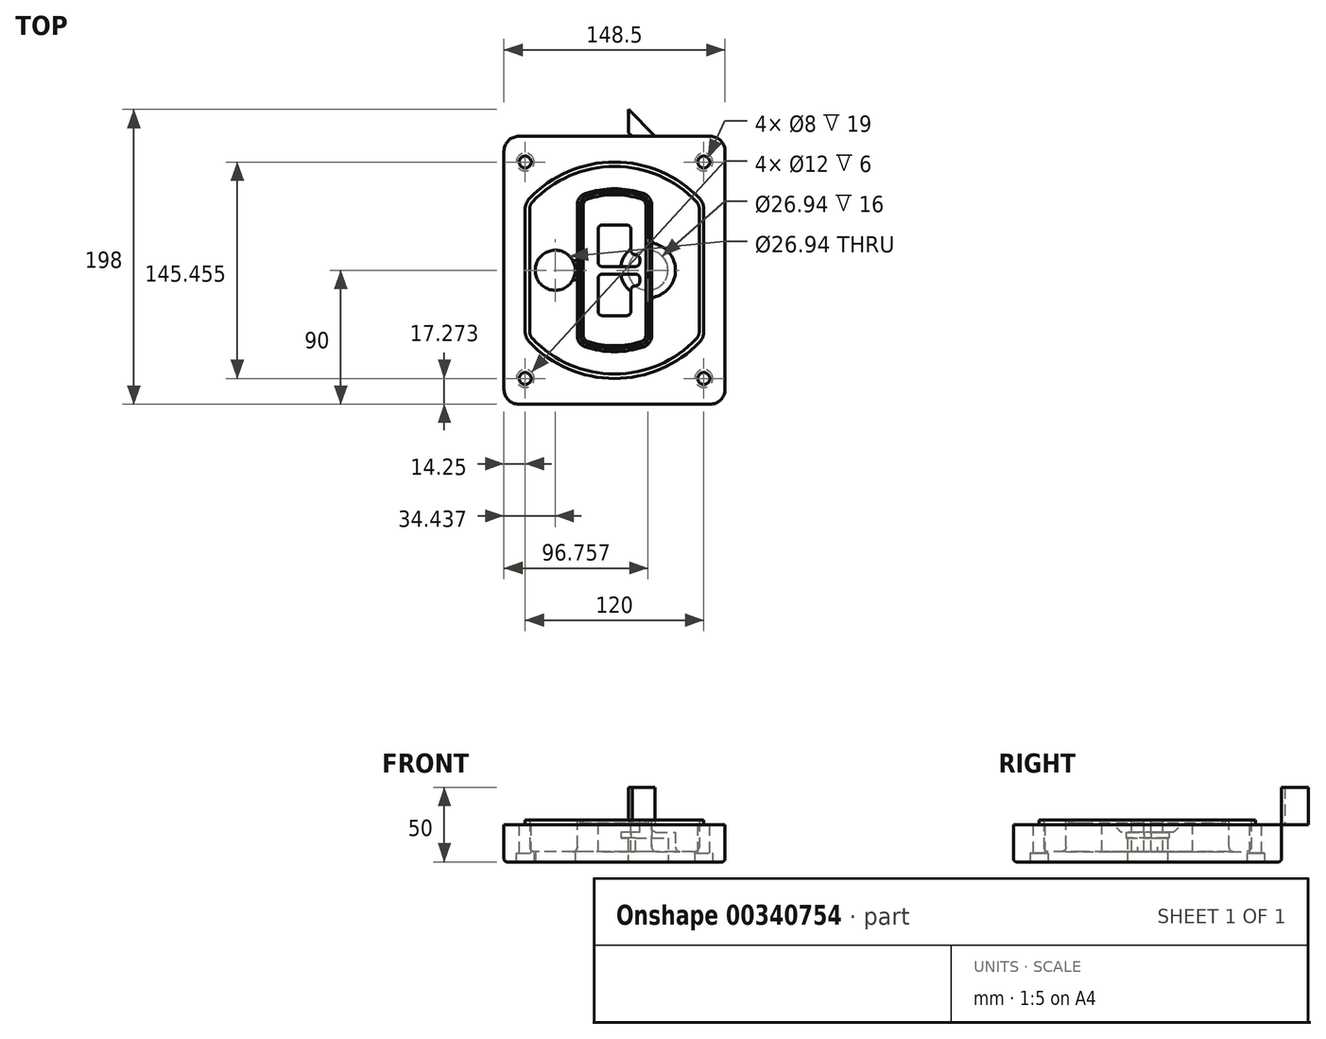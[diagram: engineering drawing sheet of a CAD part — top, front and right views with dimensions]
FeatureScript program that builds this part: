
annotation { "Feature Type Name" : "Feature", "Feature Type Description" : "" }
export const myFeature = defineFeature(function(context is Context, id is Id, definition is map)
    precondition{}
    {
        {
            var Q0;
            Q0=qCreatedBy(makeId("Top.planeOp"),FACE);
            var sketch = newSketch(context, id + "F0", { "sketchPlane" : qUnion([Q0])});
            skPoint(sketch, "E0.rect.middle", {"position": v(0, 0) * mm});
            skLineSegment(sketch, "E1.bottom", {"start": v(-64.25, -90) * mm, "end": v(64.25, -90) * mm});
            skLineSegment(sketch, "E1.top", {"start": v(-64.25, 90) * mm, "end": v(64.25, 90) * mm});
            skLineSegment(sketch, "E1.left", {"start": v(-74.25, -80) * mm, "end": v(-74.25, 80) * mm});
            skLineSegment(sketch, "E1.right", {"start": v(74.25, -80) * mm, "end": v(74.25, 80) * mm});
            skLineSegment(sketch, "E2", {"start": v(-74.25, 90) * mm, "end": v(74.25, -90) * mm, "construction": true});
            skLineSegment(sketch, "E3", {"start": v(74.25, 90) * mm, "end": v(-74.25, -90) * mm, "construction": true});
            skCircle(sketch, "E4", {"center": v(-60, 72.73) * mm, "radius": 4 * mm});
            skCircle(sketch, "E5", {"center": v(60, 72.73) * mm, "radius": 4 * mm});
            skCircle(sketch, "E6", {"center": v(60, -72.73) * mm, "radius": 4 * mm});
            skCircle(sketch, "E7", {"center": v(-60, -72.73) * mm, "radius": 4 * mm});
            skLineSegment(sketch, "E8", {"start": v(-60, 72.73) * mm, "end": v(60, 72.73) * mm, "construction": true});
            skLineSegment(sketch, "E9", {"start": v(60, 72.73) * mm, "end": v(60, -72.73) * mm, "construction": true});
            skLineSegment(sketch, "E10", {"start": v(60, -72.73) * mm, "end": v(-60, -72.73) * mm, "construction": true});
            skLineSegment(sketch, "E11", {"start": v(-60, -72.73) * mm, "end": v(-60, 72.73) * mm, "construction": true});
            skLineSegment(sketch, "E12", {"start": v(-60, 41.18) * mm, "end": v(-60, -41.18) * mm});
            skLineSegment(sketch, "E13", {"start": v(60, 41.18) * mm, "end": v(60, -41.18) * mm});
            skArc(sketch, "E14", {"start": v(57.27, 48.05) * mm, "mid": v(0, 72.73) * mm, "end": v(-57.27, 48.05) * mm});
            skArc(sketch, "E15", {"start": v(-57.27, -48.05) * mm, "mid": v(0, -72.73) * mm, "end": v(57.27, -48.05) * mm});
            skLineSegment(sketch, "E16", {"start": v(-60, 0) * mm, "end": v(60, 0) * mm, "construction": true});
            skPoint(sketch, "E17.visualSharp", {"position": v(-60, -45) * mm});
            skArc(sketch, "E17.filletArc", {"start": v(-60, -41.18) * mm, "mid": v(-59.3, -44.87) * mm, "end": v(-57.27, -48.05) * mm});
            skPoint(sketch, "E18.visualSharp", {"position": v(-60, 45) * mm});
            skArc(sketch, "E18.filletArc", {"start": v(-57.27, 48.05) * mm, "mid": v(-59.3, 44.87) * mm, "end": v(-60, 41.18) * mm});
            skPoint(sketch, "E19.visualSharp", {"position": v(60, 45) * mm});
            skArc(sketch, "E19.filletArc", {"start": v(60, 41.18) * mm, "mid": v(59.3, 44.87) * mm, "end": v(57.27, 48.05) * mm});
            skPoint(sketch, "E20.visualSharp", {"position": v(60, -45) * mm});
            skArc(sketch, "E20.filletArc", {"start": v(57.27, -48.05) * mm, "mid": v(59.3, -44.87) * mm, "end": v(60, -41.18) * mm});
            skPoint(sketch, "E21.visualSharp", {"position": v(-74.25, 90) * mm});
            skArc(sketch, "E21.filletArc", {"start": v(-64.25, 90) * mm, "mid": v(-71.32, 87.07) * mm, "end": v(-74.25, 80) * mm});
            skPoint(sketch, "E22.visualSharp", {"position": v(74.25, 90) * mm});
            skArc(sketch, "E22.filletArc", {"start": v(74.25, 80) * mm, "mid": v(71.32, 87.07) * mm, "end": v(64.25, 90) * mm});
            skPoint(sketch, "E23.visualSharp", {"position": v(74.25, -90) * mm});
            skArc(sketch, "E23.filletArc", {"start": v(64.25, -90) * mm, "mid": v(71.32, -87.07) * mm, "end": v(74.25, -80) * mm});
            skPoint(sketch, "E24.visualSharp", {"position": v(-74.25, -90) * mm});
            skArc(sketch, "E24.filletArc", {"start": v(-74.25, -80) * mm, "mid": v(-71.32, -87.07) * mm, "end": v(-64.25, -90) * mm});
            skArc(sketch, "E25.0", {"start": v(57, 41.18) * mm, "mid": v(56.5, 43.76) * mm, "end": v(55.09, 45.99) * mm});
            skLineSegment(sketch, "E25.1", {"start": v(57, 41.18) * mm, "end": v(57, -41.18) * mm});
            skArc(sketch, "E25.2", {"start": v(55.09, -45.99) * mm, "mid": v(56.5, -43.76) * mm, "end": v(57, -41.18) * mm});
            skArc(sketch, "E25.3", {"start": v(-55.09, -45.99) * mm, "mid": v(0, -69.73) * mm, "end": v(55.09, -45.99) * mm});
            skArc(sketch, "E25.4", {"start": v(-57, -41.18) * mm, "mid": v(-56.5, -43.76) * mm, "end": v(-55.09, -45.99) * mm});
            skArc(sketch, "E25.5", {"start": v(55.09, 45.99) * mm, "mid": v(0, 69.73) * mm, "end": v(-55.09, 45.99) * mm});
            skLineSegment(sketch, "E25.6", {"start": v(-57, 41.18) * mm, "end": v(-57, -41.18) * mm});
            skArc(sketch, "E25.7", {"start": v(-55.09, 45.99) * mm, "mid": v(-56.5, 43.76) * mm, "end": v(-57, 41.18) * mm});
            skArc(sketch, "E26.0", {"start": v(-60.18, 50.8) * mm, "mid": v(-63, 46.35) * mm, "end": v(-64, 41.18) * mm});
            skArc(sketch, "E26.1", {"start": v(60.18, 50.8) * mm, "mid": v(0, 76.73) * mm, "end": v(-60.18, 50.8) * mm});
            skArc(sketch, "E26.2", {"start": v(64, 41.18) * mm, "mid": v(63, 46.35) * mm, "end": v(60.18, 50.8) * mm});
            skLineSegment(sketch, "E26.3", {"start": v(64, 41.18) * mm, "end": v(64, -41.18) * mm});
            skArc(sketch, "E26.4", {"start": v(60.18, -50.8) * mm, "mid": v(63, -46.35) * mm, "end": v(64, -41.18) * mm});
            skLineSegment(sketch, "E26.5", {"start": v(-64, 41.18) * mm, "end": v(-64, -41.18) * mm});
            skArc(sketch, "E26.6", {"start": v(-60.18, -50.8) * mm, "mid": v(0, -76.73) * mm, "end": v(60.18, -50.8) * mm});
            skArc(sketch, "E26.7", {"start": v(-64, -41.18) * mm, "mid": v(-63, -46.35) * mm, "end": v(-60.18, -50.8) * mm});
            skSolve(sketch);
        }
        {
            var Q0;
            Q0=makeQuery(id+"F0.imprint","IMPRINT",FACE,{"disambiguationData":[TD([[makeQuery(id+"F0.imprint","IMPRINT",EDGE,{"derivedFrom":sQuery(id+"F0.wireOp",EDGE,"E1.bottom")}),1.0]])]});
            var Q1;
            Q1=makeQuery(id+"F0.imprint","IMPRINT",FACE,{"disambiguationData":[TD([[makeQuery(id+"F0.imprint","IMPRINT",EDGE,{"derivedFrom":sQuery(id+"F0.wireOp",EDGE,"E12")}),1.0]])]});
            var Q2;
            Q2=makeQuery(id+"F0.imprint","IMPRINT",FACE,{"disambiguationData":[TD([[makeQuery(id+"F0.imprint","IMPRINT",EDGE,{"derivedFrom":sQuery(id+"F0.wireOp",EDGE,"E25.0")}),1.0]])]});
            var Q3;
            Q3=makeQuery(id+"F0.imprint","IMPRINT",FACE,{"disambiguationData":[TD([[makeQuery(id+"F0.imprint","IMPRINT",EDGE,{"derivedFrom":sQuery(id+"F0.wireOp",EDGE,"E12")}),-1.0]])]});
            extrude(context, id + "F1", {"entities" : qUnion([Q0, Q1, Q2, Q3]), "oppositeDirection" : true, "depth" : 25 * mm});
        }
        {
            var Q0;
            Q0=makeQuery(id+"F0.imprint","IMPRINT",FACE,{"disambiguationData":[TD([[makeQuery(id+"F0.imprint","IMPRINT",EDGE,{"derivedFrom":sQuery(id+"F0.wireOp",EDGE,"E12")}),1.0]])]});
            extrude(context, id + "F2", {"entities" : qUnion([Q0]), "operationType" : NewBodyOperationType.ADD, "depth" : 3 * mm});
        }
        {
            var Q0;
            Q0=makeQuery(id+"F0.imprint","IMPRINT",FACE,{"disambiguationData":[TD([[makeQuery(id+"F0.imprint","IMPRINT",EDGE,{"derivedFrom":sQuery(id+"F0.wireOp",EDGE,"E25.0")}),1.0]])]});
            extrude(context, id + "F3", {"entities" : qUnion([Q0]), "operationType" : NewBodyOperationType.REMOVE, "oppositeDirection" : true, "depth" : 18 * mm});
        }
        {
            var Q0;
            Q0=makeQuery(id+"F2.opExtrude","CAP_FACE",FACE,{"disambiguationData":[OSD([sQuery(id+"F0.wireOp",EDGE,"E12"),sQuery(id+"F0.wireOp",EDGE,"E13"),sQuery(id+"F0.wireOp",EDGE,"E14"),sQuery(id+"F0.wireOp",EDGE,"E15"),sQuery(id+"F0.wireOp",EDGE,"E17.filletArc"),sQuery(id+"F0.wireOp",EDGE,"E18.filletArc"),sQuery(id+"F0.wireOp",EDGE,"E19.filletArc"),sQuery(id+"F0.wireOp",EDGE,"E20.filletArc"),sQuery(id+"F0.wireOp",EDGE,"E25.0"),sQuery(id+"F0.wireOp",EDGE,"E25.1"),sQuery(id+"F0.wireOp",EDGE,"E25.2"),sQuery(id+"F0.wireOp",EDGE,"E25.3"),sQuery(id+"F0.wireOp",EDGE,"E25.4"),sQuery(id+"F0.wireOp",EDGE,"E25.5"),sQuery(id+"F0.wireOp",EDGE,"E25.6"),sQuery(id+"F0.wireOp",EDGE,"E25.7")])],"isStart":false});
            var sketch = newSketch(context, id + "F4", { "sketchPlane" : qUnion([Q0])});
            skArc(sketch, "E27.0", {"start": v(-19.58, -51.49) * mm, "mid": v(0, -54.73) * mm, "end": v(19.58, -51.49) * mm});
            skArc(sketch, "E28.0", {"start": v(19.58, 51.49) * mm, "mid": v(0, 54.73) * mm, "end": v(-19.58, 51.49) * mm});
            skLineSegment(sketch, "E29", {"start": v(-25, 43.91) * mm, "end": v(-25, -43.91) * mm});
            skLineSegment(sketch, "E30", {"start": v(25, 43.91) * mm, "end": v(25, -43.91) * mm});
            skLineSegment(sketch, "E31", {"start": v(-25, 49.35) * mm, "end": v(25, 49.35) * mm, "construction": true});
            skLineSegment(sketch, "E32", {"start": v(-25, -49.35) * mm, "end": v(25, -49.35) * mm, "construction": true});
            skPoint(sketch, "E33.visualSharp", {"position": v(-25, 49.35) * mm});
            skArc(sketch, "E33.filletArc", {"start": v(-19.58, 51.49) * mm, "mid": v(-23.5, 48.57) * mm, "end": v(-25, 43.91) * mm});
            skPoint(sketch, "E34.visualSharp", {"position": v(25, 49.35) * mm});
            skArc(sketch, "E34.filletArc", {"start": v(25, 43.91) * mm, "mid": v(23.5, 48.57) * mm, "end": v(19.58, 51.49) * mm});
            skPoint(sketch, "E35.visualSharp", {"position": v(25, -49.35) * mm});
            skArc(sketch, "E35.filletArc", {"start": v(19.58, -51.49) * mm, "mid": v(23.5, -48.57) * mm, "end": v(25, -43.91) * mm});
            skPoint(sketch, "E36.visualSharp", {"position": v(-25, -49.35) * mm});
            skArc(sketch, "E36.filletArc", {"start": v(-25, -43.91) * mm, "mid": v(-23.5, -48.57) * mm, "end": v(-19.58, -51.49) * mm});
            skArc(sketch, "E37.0", {"start": v(55.09, 45.99) * mm, "mid": v(0, 69.73) * mm, "end": v(-55.09, 45.99) * mm});
            skArc(sketch, "E37.1", {"start": v(-55.09, 45.99) * mm, "mid": v(-56.5, 43.76) * mm, "end": v(-57, 41.18) * mm});
            skLineSegment(sketch, "E37.2", {"start": v(-57, 41.18) * mm, "end": v(-57, -41.18) * mm});
            skArc(sketch, "E37.3", {"start": v(-57, -41.18) * mm, "mid": v(-56.5, -43.76) * mm, "end": v(-55.09, -45.99) * mm});
            skArc(sketch, "E37.4", {"start": v(-55.09, -45.99) * mm, "mid": v(0, -69.73) * mm, "end": v(55.09, -45.99) * mm});
            skArc(sketch, "E37.5", {"start": v(55.09, -45.99) * mm, "mid": v(56.5, -43.76) * mm, "end": v(57, -41.18) * mm});
            skLineSegment(sketch, "E37.6", {"start": v(57, 41.18) * mm, "end": v(57, -41.18) * mm});
            skArc(sketch, "E37.7", {"start": v(57, 41.18) * mm, "mid": v(56.5, 43.76) * mm, "end": v(55.09, 45.99) * mm});
            skLineSegment(sketch, "E38.0", {"start": v(23, 43.91) * mm, "end": v(23, -43.91) * mm});
            skArc(sketch, "E38.1", {"start": v(18.93, -49.6) * mm, "mid": v(21.88, -47.4) * mm, "end": v(23, -43.91) * mm});
            skArc(sketch, "E38.2", {"start": v(-18.93, -49.6) * mm, "mid": v(0, -52.73) * mm, "end": v(18.93, -49.6) * mm});
            skArc(sketch, "E38.3", {"start": v(-23, -43.91) * mm, "mid": v(-21.88, -47.4) * mm, "end": v(-18.93, -49.6) * mm});
            skLineSegment(sketch, "E38.4", {"start": v(-23, 43.91) * mm, "end": v(-23, -43.91) * mm});
            skArc(sketch, "E38.5", {"start": v(23, 43.91) * mm, "mid": v(21.88, 47.4) * mm, "end": v(18.93, 49.6) * mm});
            skArc(sketch, "E38.6", {"start": v(-18.93, 49.6) * mm, "mid": v(-21.88, 47.4) * mm, "end": v(-23, 43.91) * mm});
            skArc(sketch, "E38.7", {"start": v(18.93, 49.6) * mm, "mid": v(0, 52.73) * mm, "end": v(-18.93, 49.6) * mm});
            skArc(sketch, "E39.0", {"start": v(21, 43.91) * mm, "mid": v(20.25, 46.24) * mm, "end": v(18.29, 47.7) * mm});
            skLineSegment(sketch, "E39.1", {"start": v(21, 43.91) * mm, "end": v(21, -43.91) * mm});
            skArc(sketch, "E39.2", {"start": v(18.29, -47.7) * mm, "mid": v(20.25, -46.24) * mm, "end": v(21, -43.91) * mm});
            skArc(sketch, "E39.3", {"start": v(-18.29, -47.7) * mm, "mid": v(0, -50.73) * mm, "end": v(18.29, -47.7) * mm});
            skArc(sketch, "E39.4", {"start": v(-21, -43.91) * mm, "mid": v(-20.25, -46.24) * mm, "end": v(-18.29, -47.7) * mm});
            skArc(sketch, "E39.5", {"start": v(18.29, 47.7) * mm, "mid": v(0, 50.73) * mm, "end": v(-18.29, 47.7) * mm});
            skLineSegment(sketch, "E39.6", {"start": v(-21, 43.91) * mm, "end": v(-21, -43.91) * mm});
            skArc(sketch, "E39.7", {"start": v(-18.29, 47.7) * mm, "mid": v(-20.25, 46.24) * mm, "end": v(-21, 43.91) * mm});
            skLineSegment(sketch, "E40", {"start": v(-25, 0) * mm, "end": v(25, 0) * mm, "construction": true});
            skLineSegment(sketch, "E41", {"start": v(-11, 5.5) * mm, "end": v(-11, 27.5) * mm});
            skLineSegment(sketch, "E42", {"start": v(-8, 30.5) * mm, "end": v(8, 30.5) * mm});
            skLineSegment(sketch, "E43", {"start": v(11, 27.5) * mm, "end": v(11, 13.5) * mm});
            skLineSegment(sketch, "E44", {"start": v(14, 10.5) * mm, "end": v(14, 10.5) * mm});
            skLineSegment(sketch, "E45", {"start": v(17, 7.5) * mm, "end": v(17, 5.5) * mm});
            skLineSegment(sketch, "E46", {"start": v(14, 2.5) * mm, "end": v(-8, 2.5) * mm});
            skPoint(sketch, "E47.visualSharp", {"position": v(-11, 30.5) * mm});
            skArc(sketch, "E47.filletArc", {"start": v(-8, 30.5) * mm, "mid": v(-10.12, 29.62) * mm, "end": v(-11, 27.5) * mm});
            skPoint(sketch, "E48.visualSharp", {"position": v(11, 30.5) * mm});
            skArc(sketch, "E48.filletArc", {"start": v(11, 27.5) * mm, "mid": v(10.12, 29.62) * mm, "end": v(8, 30.5) * mm});
            skPoint(sketch, "E49.visualSharp", {"position": v(11, 10.5) * mm});
            skArc(sketch, "E49.filletArc", {"start": v(11, 13.5) * mm, "mid": v(11.88, 11.38) * mm, "end": v(14, 10.5) * mm});
            skPoint(sketch, "E50.visualSharp", {"position": v(17, 10.5) * mm});
            skArc(sketch, "E50.filletArc", {"start": v(17, 7.5) * mm, "mid": v(16.12, 9.62) * mm, "end": v(14, 10.5) * mm});
            skPoint(sketch, "E51.visualSharp", {"position": v(17, 2.5) * mm});
            skArc(sketch, "E51.filletArc", {"start": v(14, 2.5) * mm, "mid": v(16.12, 3.38) * mm, "end": v(17, 5.5) * mm});
            skPoint(sketch, "E52.visualSharp", {"position": v(-11, 2.5) * mm});
            skArc(sketch, "E52.filletArc", {"start": v(-11, 5.5) * mm, "mid": v(-10.12, 3.38) * mm, "end": v(-8, 2.5) * mm});
            skLineSegment(sketch, "E53.0.MirrorCS", {"start": v(14, -2.5) * mm, "end": v(-8, -2.5) * mm});
            skArc(sketch, "E54.0.MirrorCS", {"start": v(-11, -5.5) * mm, "mid": v(-10.12, -3.38) * mm, "end": v(-8, -2.5) * mm});
            skLineSegment(sketch, "E55.0.MirrorCS", {"start": v(-11, -5.5) * mm, "end": v(-11, -27.5) * mm});
            skArc(sketch, "E56.0.MirrorCS", {"start": v(-8, -30.5) * mm, "mid": v(-10.12, -29.62) * mm, "end": v(-11, -27.5) * mm});
            skLineSegment(sketch, "E57.0.MirrorCS", {"start": v(-8, -30.5) * mm, "end": v(8, -30.5) * mm});
            skArc(sketch, "E58.0.MirrorCS", {"start": v(11, -27.5) * mm, "mid": v(10.12, -29.62) * mm, "end": v(8, -30.5) * mm});
            skLineSegment(sketch, "E59.0.MirrorCS", {"start": v(11, -27.5) * mm, "end": v(11, -13.5) * mm});
            skArc(sketch, "E60.0.MirrorCS", {"start": v(11, -13.5) * mm, "mid": v(11.88, -11.38) * mm, "end": v(14, -10.5) * mm});
            skArc(sketch, "E61.0.MirrorCS", {"start": v(17, -7.5) * mm, "mid": v(16.12, -9.62) * mm, "end": v(14, -10.5) * mm});
            skLineSegment(sketch, "E62.0.MirrorCS", {"start": v(17, -7.5) * mm, "end": v(17, -5.5) * mm});
            skArc(sketch, "E63.0.MirrorCS", {"start": v(14, -2.5) * mm, "mid": v(16.12, -3.38) * mm, "end": v(17, -5.5) * mm});
            skSolve(sketch);
        }
        {
            var Q0;
            Q0=makeQuery(id+"F4.imprint","IMPRINT",FACE,{"disambiguationData":[TD([[makeQuery(id+"F4.imprint","IMPRINT",EDGE,{"derivedFrom":sQuery(id+"F4.wireOp",EDGE,"E27.0")}),1.0]])]});
            var Q1;
            Q1=makeQuery(id+"F4.imprint","IMPRINT",FACE,{"disambiguationData":[TD([[makeQuery(id+"F4.imprint","IMPRINT",EDGE,{"derivedFrom":sQuery(id+"F4.wireOp",EDGE,"E38.0")}),-1.0]])]});
            var Q2;
            Q2=makeQuery(id+"F4.imprint","IMPRINT",FACE,{"disambiguationData":[TD([[makeQuery(id+"F4.imprint","IMPRINT",EDGE,{"derivedFrom":sQuery(id+"F4.wireOp",EDGE,"E39.0")}),1.0]])]});
            extrude(context, id + "F5", {"entities" : qUnion([Q0, Q1, Q2]), "operationType" : NewBodyOperationType.ADD, "endBound" : BoundingType.UP_TO_NEXT, "oppositeDirection" : true, "depth" : 25 * mm});
        }
        {
            var Q0;
            Q0=makeQuery(id+"F4.imprint","IMPRINT",FACE,{"disambiguationData":[TD([[makeQuery(id+"F4.imprint","IMPRINT",EDGE,{"derivedFrom":sQuery(id+"F4.wireOp",EDGE,"E38.0")}),-1.0]])]});
            extrude(context, id + "F6", {"entities" : qUnion([Q0]), "operationType" : NewBodyOperationType.REMOVE, "oppositeDirection" : true, "depth" : 2 * mm});
        }
        {
            var Q0;
            Q0=makeQuery(id+"F1.opExtrude","CAP_FACE",FACE,{"disambiguationData":[OSD([sQuery(id+"F0.wireOp",EDGE,"E1.bottom"),sQuery(id+"F0.wireOp",EDGE,"E1.top"),sQuery(id+"F0.wireOp",EDGE,"E1.left"),sQuery(id+"F0.wireOp",EDGE,"E1.right"),sQuery(id+"F0.wireOp",EDGE,"E4"),sQuery(id+"F0.wireOp",EDGE,"E5"),sQuery(id+"F0.wireOp",EDGE,"E6"),sQuery(id+"F0.wireOp",EDGE,"E7"),sQuery(id+"F0.wireOp",EDGE,"E21.filletArc"),sQuery(id+"F0.wireOp",EDGE,"E22.filletArc"),sQuery(id+"F0.wireOp",EDGE,"E23.filletArc"),sQuery(id+"F0.wireOp",EDGE,"E24.filletArc")])],"isStart":false});
            var sketch = newSketch(context, id + "F7", { "sketchPlane" : qUnion([Q0])});
            skCircle(sketch, "E64", {"center": v(22.5, 0) * mm, "radius": 13.47 * mm});
            skCircle(sketch, "E65", {"center": v(-39.81, 0) * mm, "radius": 13.47 * mm});
            skLineSegment(sketch, "E66", {"start": v(74.25, 0) * mm, "end": v(-74.25, 0) * mm});
            skCircle(sketch, "E67", {"center": v(22.5, 0) * mm, "radius": 18.47 * mm});
            skCircle(sketch, "E68", {"center": v(60, -72.73) * mm, "radius": 6 * mm});
            skCircle(sketch, "E69", {"center": v(-60, -72.73) * mm, "radius": 6 * mm});
            skCircle(sketch, "E70", {"center": v(-60, 72.73) * mm, "radius": 6 * mm});
            skCircle(sketch, "E71", {"center": v(60, 72.73) * mm, "radius": 6 * mm});
            skSolve(sketch);
        }
        {
            var Q0;
            {var subQ1=sQuery(id+"F7.wireOp",EDGE,"E66");var subQ4=sQuery(id+"F7.wireOp",EDGE,"E64");var subQ6=makeQuery(id+"F7.imprint","INTERSECT",VERTEX,{"disambiguationData":[OD(0.0)],"derivedFrom":[subQ4,subQ1]});Q0=makeQuery(id+"F7.imprint","IMPRINT",FACE,{"disambiguationData":[TD([[makeQuery(id+"F7.imprint","IMPRINT",EDGE,{"disambiguationData":[TD([[subQ6,-1.0]])],"derivedFrom":subQ4}),-1.0]])]});}
            var Q1;
            {var subQ0=sQuery(id+"F7.wireOp",EDGE,"E66");var subQ1=sQuery(id+"F7.wireOp",EDGE,"E64");var subQ3=makeQuery(id+"F7.imprint","INTERSECT",VERTEX,{"disambiguationData":[OD(0.0)],"derivedFrom":[subQ1,subQ0]});Q1=makeQuery(id+"F7.imprint","IMPRINT",FACE,{"disambiguationData":[TD([[makeQuery(id+"F7.imprint","IMPRINT",EDGE,{"disambiguationData":[TD([[subQ3,-1.0]])],"derivedFrom":subQ1}),1.0]])]});}
            var Q2;
            {var subQ0=sQuery(id+"F7.wireOp",EDGE,"E66");var subQ1=sQuery(id+"F7.wireOp",EDGE,"E64");var subQ3=makeQuery(id+"F7.imprint","INTERSECT",VERTEX,{"disambiguationData":[OD(0.0)],"derivedFrom":[subQ1,subQ0]});Q2=makeQuery(id+"F7.imprint","IMPRINT",FACE,{"disambiguationData":[TD([[makeQuery(id+"F7.imprint","IMPRINT",EDGE,{"disambiguationData":[TD([[subQ3,1.0]])],"derivedFrom":subQ1}),1.0]])]});}
            var Q3;
            {var subQ1=sQuery(id+"F7.wireOp",EDGE,"E66");var subQ4=sQuery(id+"F7.wireOp",EDGE,"E64");var subQ6=makeQuery(id+"F7.imprint","INTERSECT",VERTEX,{"disambiguationData":[OD(0.0)],"derivedFrom":[subQ4,subQ1]});Q3=makeQuery(id+"F7.imprint","IMPRINT",FACE,{"disambiguationData":[TD([[makeQuery(id+"F7.imprint","IMPRINT",EDGE,{"disambiguationData":[TD([[subQ6,1.0]])],"derivedFrom":subQ4}),-1.0]])]});}
            extrude(context, id + "F8", {"entities" : qUnion([Q0, Q1, Q2, Q3]), "operationType" : NewBodyOperationType.ADD, "oppositeDirection" : true, "depth" : 20 * mm});
        }
        {
            var Q0;
            {var subQ0=sQuery(id+"F7.wireOp",EDGE,"E66");var subQ1=sQuery(id+"F7.wireOp",EDGE,"E64");var subQ3=makeQuery(id+"F7.imprint","INTERSECT",VERTEX,{"disambiguationData":[OD(0.0)],"derivedFrom":[subQ1,subQ0]});Q0=makeQuery(id+"F7.imprint","IMPRINT",FACE,{"disambiguationData":[TD([[makeQuery(id+"F7.imprint","IMPRINT",EDGE,{"disambiguationData":[TD([[subQ3,-1.0]])],"derivedFrom":subQ1}),1.0]])]});}
            var Q1;
            {var subQ0=sQuery(id+"F7.wireOp",EDGE,"E66");var subQ1=sQuery(id+"F7.wireOp",EDGE,"E64");var subQ3=makeQuery(id+"F7.imprint","INTERSECT",VERTEX,{"disambiguationData":[OD(0.0)],"derivedFrom":[subQ1,subQ0]});Q1=makeQuery(id+"F7.imprint","IMPRINT",FACE,{"disambiguationData":[TD([[makeQuery(id+"F7.imprint","IMPRINT",EDGE,{"disambiguationData":[TD([[subQ3,1.0]])],"derivedFrom":subQ1}),1.0]])]});}
            extrude(context, id + "F9", {"entities" : qUnion([Q0, Q1]), "operationType" : NewBodyOperationType.REMOVE, "oppositeDirection" : true, "depth" : 16 * mm});
        }
        {
            var Q0;
            {var subQ0=sQuery(id+"F7.wireOp",EDGE,"E66");var subQ1=sQuery(id+"F7.wireOp",EDGE,"E65");var subQ3=makeQuery(id+"F7.imprint","INTERSECT",VERTEX,{"disambiguationData":[OD(0.0)],"derivedFrom":[subQ1,subQ0]});Q0=makeQuery(id+"F7.imprint","IMPRINT",FACE,{"disambiguationData":[TD([[makeQuery(id+"F7.imprint","IMPRINT",EDGE,{"disambiguationData":[TD([[subQ3,-1.0]])],"derivedFrom":subQ1}),1.0]])]});}
            var Q1;
            {var subQ0=sQuery(id+"F7.wireOp",EDGE,"E66");var subQ1=sQuery(id+"F7.wireOp",EDGE,"E65");var subQ3=makeQuery(id+"F7.imprint","INTERSECT",VERTEX,{"disambiguationData":[OD(0.0)],"derivedFrom":[subQ1,subQ0]});Q1=makeQuery(id+"F7.imprint","IMPRINT",FACE,{"disambiguationData":[TD([[makeQuery(id+"F7.imprint","IMPRINT",EDGE,{"disambiguationData":[TD([[subQ3,1.0]])],"derivedFrom":subQ1}),1.0]])]});}
            extrude(context, id + "F10", {"entities" : qUnion([Q0, Q1]), "operationType" : NewBodyOperationType.REMOVE, "oppositeDirection" : true, "depth" : 25 * mm});
        }
        {
            var Q0;
            Q0=makeQuery(id+"F7.imprint","IMPRINT",FACE,{"disambiguationData":[TD([[makeQuery(id+"F7.imprint","IMPRINT",EDGE,{"derivedFrom":sQuery(id+"F7.wireOp",EDGE,"E68")}),1.0]])]});
            var Q1;
            Q1=makeQuery(id+"F7.imprint","IMPRINT",FACE,{"disambiguationData":[TD([[makeQuery(id+"F7.imprint","IMPRINT",EDGE,{"derivedFrom":makeQuery(id+"F1.opExtrude","CAP_EDGE",EDGE,{"disambiguationData":[OSD([sQuery(id+"F0.wireOp",EDGE,"E5")])],"isStart":false})}),-1.0]])]});
            var Q2;
            Q2=makeQuery(id+"F7.imprint","IMPRINT",FACE,{"disambiguationData":[TD([[makeQuery(id+"F7.imprint","IMPRINT",EDGE,{"derivedFrom":sQuery(id+"F7.wireOp",EDGE,"E69")}),1.0]])]});
            var Q3;
            Q3=makeQuery(id+"F7.imprint","IMPRINT",FACE,{"disambiguationData":[TD([[makeQuery(id+"F7.imprint","IMPRINT",EDGE,{"derivedFrom":makeQuery(id+"F1.opExtrude","CAP_EDGE",EDGE,{"disambiguationData":[OSD([sQuery(id+"F0.wireOp",EDGE,"E4")])],"isStart":false})}),-1.0]])]});
            var Q4;
            Q4=makeQuery(id+"F7.imprint","IMPRINT",FACE,{"disambiguationData":[TD([[makeQuery(id+"F7.imprint","IMPRINT",EDGE,{"derivedFrom":sQuery(id+"F7.wireOp",EDGE,"E70")}),1.0]])]});
            var Q5;
            Q5=makeQuery(id+"F7.imprint","IMPRINT",FACE,{"disambiguationData":[TD([[makeQuery(id+"F7.imprint","IMPRINT",EDGE,{"derivedFrom":makeQuery(id+"F1.opExtrude","CAP_EDGE",EDGE,{"disambiguationData":[OSD([sQuery(id+"F0.wireOp",EDGE,"E7")])],"isStart":false})}),-1.0]])]});
            var Q6;
            Q6=makeQuery(id+"F7.imprint","IMPRINT",FACE,{"disambiguationData":[TD([[makeQuery(id+"F7.imprint","IMPRINT",EDGE,{"derivedFrom":sQuery(id+"F7.wireOp",EDGE,"E71")}),1.0]])]});
            var Q7;
            Q7=makeQuery(id+"F7.imprint","IMPRINT",FACE,{"disambiguationData":[TD([[makeQuery(id+"F7.imprint","IMPRINT",EDGE,{"derivedFrom":makeQuery(id+"F1.opExtrude","CAP_EDGE",EDGE,{"disambiguationData":[OSD([sQuery(id+"F0.wireOp",EDGE,"E6")])],"isStart":false})}),-1.0]])]});
            extrude(context, id + "F11", {"entities" : qUnion([Q0, Q1, Q2, Q3, Q4, Q5, Q6, Q7]), "operationType" : NewBodyOperationType.REMOVE, "oppositeDirection" : true, "depth" : 6 * mm});
        }
        {
            var Q0;
            Q0=makeQuery(id+"F9.boolean.opBoolean","COPY",FACE,{"derivedFrom":makeQuery(id+"F9.opExtrude","CAP_FACE",FACE,{"disambiguationData":[OSD([sQuery(id+"F7.wireOp",EDGE,"E64")])],"isStart":false})});
            var sketch = newSketch(context, id + "F12", { "sketchPlane" : qUnion([Q0])});
            skArc(sketch, "E72.0", {"start": v(11, 14.45) * mm, "mid": v(6.45, 9.13) * mm, "end": v(4.2, 2.5) * mm});
            skArc(sketch, "E72.1", {"start": v(4.2, -2.5) * mm, "mid": v(6.45, -9.13) * mm, "end": v(11, -14.45) * mm});
            skLineSegment(sketch, "E73", {"start": v(4.2, -2.5) * mm, "end": v(14, -2.5) * mm});
            skLineSegment(sketch, "E74.0", {"start": v(14, 2.5) * mm, "end": v(4.2, 2.5) * mm});
            skArc(sketch, "E74.1", {"start": v(14, 2.5) * mm, "mid": v(16.12, 3.38) * mm, "end": v(17, 5.5) * mm});
            skLineSegment(sketch, "E74.2", {"start": v(17, 7.5) * mm, "end": v(17, 5.5) * mm});
            skArc(sketch, "E74.3", {"start": v(17, 7.5) * mm, "mid": v(16.12, 9.62) * mm, "end": v(14, 10.5) * mm});
            skArc(sketch, "E74.4", {"start": v(11, 13.5) * mm, "mid": v(11.88, 11.38) * mm, "end": v(14, 10.5) * mm});
            skLineSegment(sketch, "E74.5", {"start": v(11, 14.45) * mm, "end": v(11, 13.5) * mm});
            skLineSegment(sketch, "E74.7", {"start": v(14, -2.5) * mm, "end": v(4.2, -2.5) * mm});
            skArc(sketch, "E74.8", {"start": v(14, -2.5) * mm, "mid": v(16.12, -3.38) * mm, "end": v(17, -5.5) * mm});
            skLineSegment(sketch, "E74.9", {"start": v(17, -7.5) * mm, "end": v(17, -5.5) * mm});
            skArc(sketch, "E74.10", {"start": v(17, -7.5) * mm, "mid": v(16.12, -9.62) * mm, "end": v(14, -10.5) * mm});
            skArc(sketch, "E74.11", {"start": v(11, -13.5) * mm, "mid": v(11.88, -11.38) * mm, "end": v(14, -10.5) * mm});
            skLineSegment(sketch, "E74.12", {"start": v(11, -14.45) * mm, "end": v(11, -13.5) * mm});
            skPoint(sketch, "E75.orphan", {"position": v(11, -27.5) * mm});
            skPoint(sketch, "E76.orphan", {"position": v(-8, -2.5) * mm});
            skPoint(sketch, "E77.orphan", {"position": v(-8, 2.5) * mm});
            skPoint(sketch, "E78.orphan", {"position": v(11, 27.5) * mm});
            skSolve(sketch);
        }
        {
            var Q0;
            {var subQ7=sQuery(id+"F12.wireOp",EDGE,"E72.0");var subQ14=sQuery(id+"F12.wireOp",EDGE,"E72.1");var subQ16=sQuery(id+"F12.wireOp",EDGE,"E74.1");var subQ18=sQuery(id+"F12.wireOp",EDGE,"E74.8");Q0=qUnion([makeQuery(id+"F12.imprint","IMPRINT",FACE,{"disambiguationData":[TD([[makeQuery(id+"F12.imprint","IMPRINT",EDGE,{"derivedFrom":subQ7}),1.0]])]}),makeQuery(id+"F12.imprint","IMPRINT",FACE,{"disambiguationData":[TD([[makeQuery(id+"F12.imprint","IMPRINT",EDGE,{"derivedFrom":subQ14}),1.0]])]}),makeQuery(id+"F12.imprint","IMPRINT",FACE,{"disambiguationData":[TD([[makeQuery(id+"F12.imprint","IMPRINT",EDGE,{"derivedFrom":subQ16}),1.0]])]}),makeQuery(id+"F12.imprint","IMPRINT",FACE,{"disambiguationData":[TD([[makeQuery(id+"F12.imprint","IMPRINT",EDGE,{"derivedFrom":subQ18}),-1.0]])]})]);}
            var Q1;
            Q1=makeQuery(id+"F5.boolean.opBoolean","SPLIT",FACE,{"disambiguationData":[TD([makeQuery(id+"F5.opExtrude","SWEPT_FACE",FACE,{"disambiguationData":[OSD([sQuery(id+"F4.wireOp",EDGE,"E41")])]})])],"derivedFrom":makeQuery(id+"F3.boolean.opBoolean","COPY",FACE,{"derivedFrom":makeQuery(id+"F3.opExtrude","CAP_FACE",FACE,{"disambiguationData":[OSD([sQuery(id+"F0.wireOp",EDGE,"E25.0"),sQuery(id+"F0.wireOp",EDGE,"E25.1"),sQuery(id+"F0.wireOp",EDGE,"E25.2"),sQuery(id+"F0.wireOp",EDGE,"E25.3"),sQuery(id+"F0.wireOp",EDGE,"E25.4"),sQuery(id+"F0.wireOp",EDGE,"E25.5"),sQuery(id+"F0.wireOp",EDGE,"E25.6"),sQuery(id+"F0.wireOp",EDGE,"E25.7")])],"isStart":false})})});
            extrude(context, id + "F13", {"entities" : qUnion([Q0]), "operationType" : NewBodyOperationType.REMOVE, "endBound" : BoundingType.UP_TO_SURFACE, "endBoundEntityFace" : qUnion([Q1]), "depth" : 25 * mm});
        }
        {
            var Q0;
            Q0=makeQuery(id+"F3.boolean.opBoolean","COPY",EDGE,{"derivedFrom":makeQuery(id+"F3.opExtrude","CAP_EDGE",EDGE,{"disambiguationData":[OSD([sQuery(id+"F0.wireOp",EDGE,"E25.6")])],"isStart":false})});
            var Q1;
            Q1=makeQuery(id+"F8.boolean.opBoolean","INTERSECT",EDGE,{"derivedFrom":[makeQuery(id+"F5.opExtrude","SWEPT_FACE",FACE,{"disambiguationData":[OSD([sQuery(id+"F4.wireOp",EDGE,"E30")])]}),makeQuery(id+"F8.opExtrude","CAP_FACE",FACE,{"disambiguationData":[OSD([sQuery(id+"F7.wireOp",EDGE,"E67")])],"isStart":false})]});
            var Q2;
            Q2=makeQuery(id+"F8.boolean.opBoolean","INTERSECT",EDGE,{"disambiguationData":[OD(1.0)],"derivedFrom":[makeQuery(id+"F5.opExtrude","SWEPT_FACE",FACE,{"disambiguationData":[OSD([sQuery(id+"F4.wireOp",EDGE,"E30")])]}),makeQuery(id+"F8.opExtrude","SWEPT_FACE",FACE,{"disambiguationData":[OSD([sQuery(id+"F7.wireOp",EDGE,"E67")])]})]});
            var Q3;
            {var subQ0=sQuery(id+"F4.wireOp",EDGE,"E30");Q3=makeQuery(id+"F8.boolean.opBoolean","SPLIT",EDGE,{"disambiguationData":[TD([makeQuery(id+"F5.opExtrude","SWEPT_FACE",FACE,{"disambiguationData":[OSD([sQuery(id+"F4.wireOp",EDGE,"E35.filletArc")])]})])],"derivedFrom":makeQuery(id+"F5.opExtrude","CAP_EDGE",EDGE,{"disambiguationData":[OSD([subQ0])],"isStart":false})});}
            var Q4;
            {var subQ0=sQuery(id+"F0.wireOp",EDGE,"E25.7");var subQ1=sQuery(id+"F0.wireOp",EDGE,"E25.1");var subQ2=sQuery(id+"F0.wireOp",EDGE,"E25.6");var subQ3=sQuery(id+"F0.wireOp",EDGE,"E25.5");var subQ4=sQuery(id+"F0.wireOp",EDGE,"E25.4");var subQ5=sQuery(id+"F0.wireOp",EDGE,"E25.0");var subQ6=sQuery(id+"F0.wireOp",EDGE,"E25.2");var subQ7=sQuery(id+"F0.wireOp",EDGE,"E25.3");Q4=makeQuery(id+"F8.boolean.opBoolean","INTERSECT",EDGE,{"derivedFrom":[makeQuery(id+"F5.boolean.opBoolean","SPLIT",FACE,{"disambiguationData":[TD([makeQuery(id+"F2.opExtrude","SWEPT_FACE",FACE,{"disambiguationData":[OSD([subQ5])]})])],"derivedFrom":makeQuery(id+"F3.boolean.opBoolean","COPY",FACE,{"derivedFrom":makeQuery(id+"F3.opExtrude","CAP_FACE",FACE,{"disambiguationData":[OSD([subQ5,subQ1,subQ6,subQ7,subQ4,subQ3,subQ2,subQ0])],"isStart":false})})}),makeQuery(id+"F8.opExtrude","SWEPT_FACE",FACE,{"disambiguationData":[OSD([sQuery(id+"F7.wireOp",EDGE,"E67")])]})]});}
            var Q5;
            Q5=makeQuery(id+"F8.boolean.opBoolean","INTERSECT",EDGE,{"disambiguationData":[OD(0.0)],"derivedFrom":[makeQuery(id+"F5.opExtrude","SWEPT_FACE",FACE,{"disambiguationData":[OSD([sQuery(id+"F4.wireOp",EDGE,"E30")])]}),makeQuery(id+"F8.opExtrude","SWEPT_FACE",FACE,{"disambiguationData":[OSD([sQuery(id+"F7.wireOp",EDGE,"E67")])]})]});
            fillet(context, id + "F14", {"entities" : qUnion([Q0, Q1, Q2, Q3, Q4, Q5]), "radius" : 3 * mm, "tangentPropagation" : true, "allowEdgeOverflow" : false});
        }
        {
            var Q0;
            Q0=makeQuery(id+"F1.opExtrude","CAP_EDGE",EDGE,{"disambiguationData":[OSD([sQuery(id+"F0.wireOp",EDGE,"E1.bottom")])],"isStart":false});
            fillet(context, id + "F15", {"entities" : qUnion([Q0]), "radius" : 2 * mm, "tangentPropagation" : true, "allowEdgeOverflow" : false});
        }
        {
            var Q0;
            {var subQ0=sQuery(id+"F0.wireOp",EDGE,"E21.filletArc");var subQ1=sQuery(id+"F0.wireOp",EDGE,"E7");var subQ2=sQuery(id+"F0.wireOp",EDGE,"E6");var subQ3=sQuery(id+"F0.wireOp",EDGE,"E5");var subQ4=sQuery(id+"F0.wireOp",EDGE,"E4");var subQ5=sQuery(id+"F0.wireOp",EDGE,"E22.filletArc");var subQ6=sQuery(id+"F0.wireOp",EDGE,"E1.bottom");var subQ7=sQuery(id+"F0.wireOp",EDGE,"E1.right");var subQ8=sQuery(id+"F0.wireOp",EDGE,"E1.top");var subQ9=sQuery(id+"F0.wireOp",EDGE,"E1.left");var subQ10=sQuery(id+"F0.wireOp",EDGE,"E23.filletArc");var subQ11=sQuery(id+"F0.wireOp",EDGE,"E24.filletArc");Q0=makeQuery(id+"F2.boolean.opBoolean","SPLIT",FACE,{"disambiguationData":[TD([makeQuery(id+"F1.opExtrude","SWEPT_FACE",FACE,{"disambiguationData":[OSD([subQ6])]})])],"derivedFrom":makeQuery(id+"F1.opExtrude","CAP_FACE",FACE,{"disambiguationData":[OSD([subQ6,subQ8,subQ9,subQ7,subQ4,subQ3,subQ2,subQ1,subQ0,subQ5,subQ10,subQ11])],"isStart":true})});}
            var sketch = newSketch(context, id + "F16", { "sketchPlane" : qUnion([Q0])});
            skLineSegment(sketch, "E79", {"start": v(-38.35, 90) * mm, "end": v(-20.55, 108) * mm});
            skLineSegment(sketch, "E80", {"start": v(11.84, 90) * mm, "end": v(9.45, 92.39) * mm});
            skLineSegment(sketch, "E81", {"start": v(-20.55, 108) * mm, "end": v(-20.55, 120) * mm});
            skLineSegment(sketch, "E82", {"start": v(9.45, 92.39) * mm, "end": v(9.45, 120) * mm});
            skArc(sketch, "E83", {"start": v(9.45, 120) * mm, "mid": v(-5.55, 135) * mm, "end": v(-20.55, 120) * mm});
            skCircle(sketch, "E84", {"center": v(-5.55, 120) * mm, "radius": 6 * mm});
            skLineSegment(sketch, "E85", {"start": v(-5.55, 120) * mm, "end": v(-5.55, 90) * mm, "construction": true});
            skLineSegment(sketch, "E86", {"start": v(-74.25, 0) * mm, "end": v(74.25, 0) * mm, "construction": true});
            skLineSegment(sketch, "E87.MirrorCS", {"start": v(-20.55, 92.39) * mm, "end": v(-20.55, 120) * mm});
            skLineSegment(sketch, "E88.MirrorCS", {"start": v(-22.94, 90) * mm, "end": v(-20.55, 92.39) * mm});
            skArc(sketch, "E89.MirrorCS", {"start": v(-20.55, 120) * mm, "mid": v(-5.55, 135) * mm, "end": v(9.45, 120) * mm});
            skLineSegment(sketch, "E90.MirrorCS", {"start": v(27.26, 90) * mm, "end": v(9.45, 108) * mm});
            skLineSegment(sketch, "E91.MirrorCS", {"start": v(9.45, 108) * mm, "end": v(9.45, 120) * mm});
            skLineSegment(sketch, "E92.MirrorCS", {"start": v(63.15, 0) * mm, "end": v(-74.25, 0) * mm, "construction": true});
            skLineSegment(sketch, "E93.MirrorCS", {"start": v(11.84, -90) * mm, "end": v(9.45, -92.39) * mm});
            skLineSegment(sketch, "E94.MirrorCS", {"start": v(9.45, -108) * mm, "end": v(9.45, -120) * mm});
            skArc(sketch, "E95.MirrorCS", {"start": v(9.45, -120) * mm, "mid": v(-5.55, -135) * mm, "end": v(-20.55, -120) * mm});
            skLineSegment(sketch, "E96.MirrorCS", {"start": v(-20.55, -92.39) * mm, "end": v(-20.55, -120) * mm});
            skLineSegment(sketch, "E97.MirrorCS", {"start": v(-38.35, -90) * mm, "end": v(-20.55, -108) * mm});
            skCircle(sketch, "E98.MirrorC", {"center": v(-5.55, -120) * mm, "radius": 6 * mm});
            skPoint(sketch, "E99.orphan", {"position": v(-85.35, 0) * mm});
            skLineSegment(sketch, "E100.MirrorCS", {"start": v(-5.55, -120) * mm, "end": v(-5.55, -90) * mm, "construction": true});
            skLineSegment(sketch, "E101.MirrorCS", {"start": v(9.45, -92.39) * mm, "end": v(9.45, -120) * mm});
            skLineSegment(sketch, "E102.MirrorCS", {"start": v(27.26, -90) * mm, "end": v(9.45, -108) * mm});
            skSolve(sketch);
        }
        {
            var Q0;
            {var subQ1=sQuery(id+"F16.wireOp",EDGE,"E90.MirrorCS");Q0=makeQuery(id+"F16.imprint","IMPRINT",FACE,{"disambiguationData":[TD([[makeQuery(id+"F16.imprint","IMPRINT",EDGE,{"derivedFrom":subQ1}),1.0]])]});}
            extrude(context, id + "F17", {"entities" : qUnion([Q0]), "depth" : 25 * mm});
        }
    });
